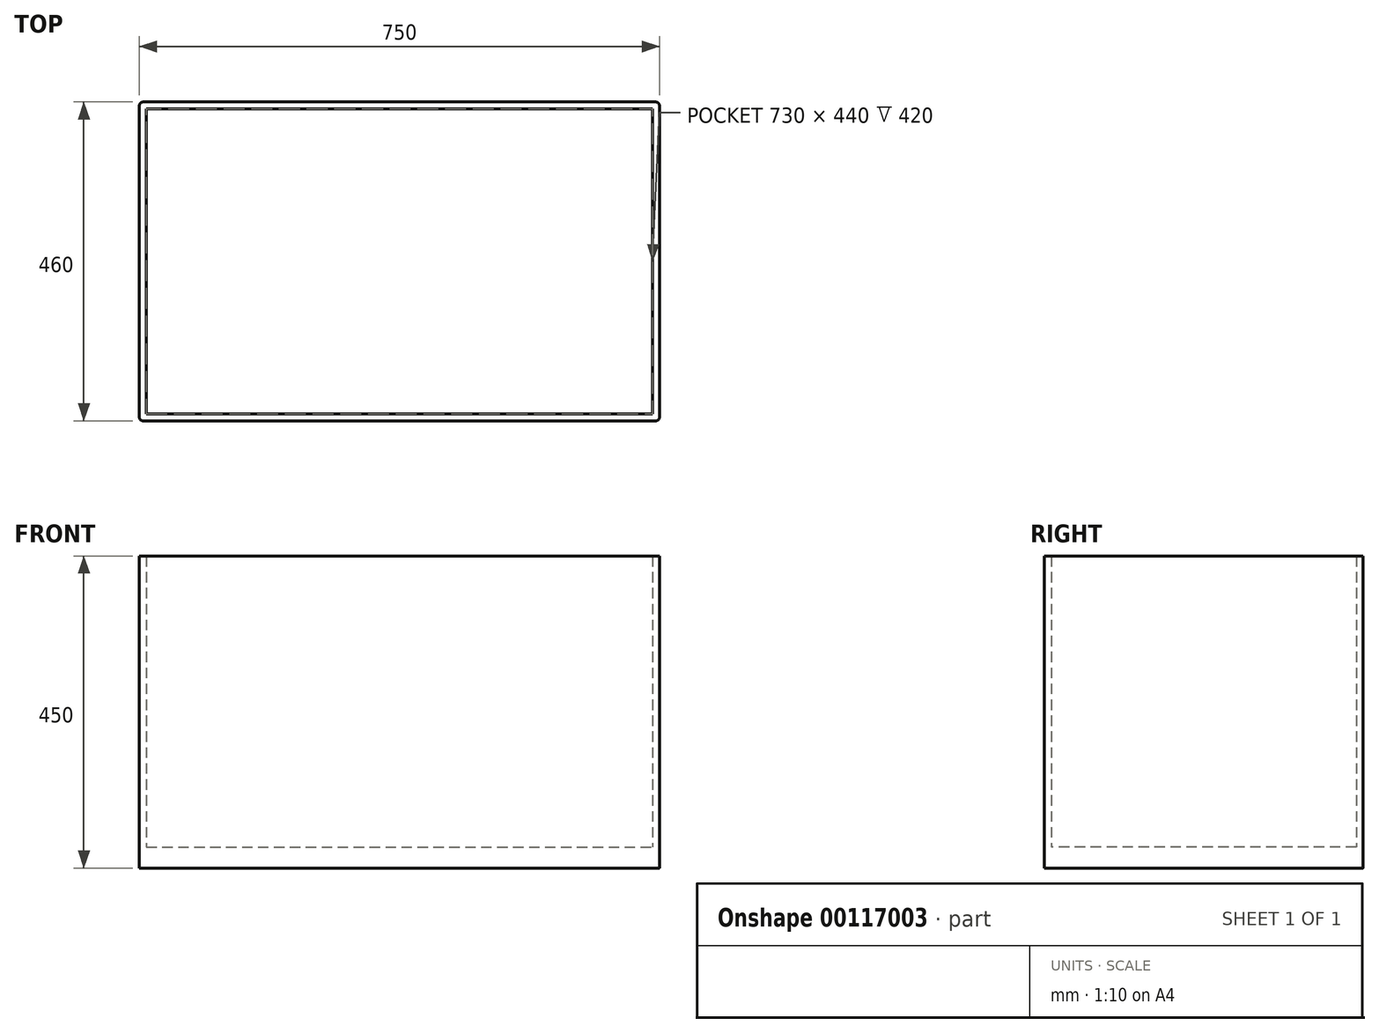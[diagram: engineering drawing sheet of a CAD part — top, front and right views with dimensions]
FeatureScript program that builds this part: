
annotation { "Feature Type Name" : "Feature", "Feature Type Description" : "" }
export const myFeature = defineFeature(function(context is Context, id is Id, definition is map)
    precondition{}
    {
        {
            var Q0;
            Q0=qCreatedBy(makeId("Top.planeOp"),FACE);
            var sketch = newSketch(context, id + "F0", { "sketchPlane" : qUnion([Q0])});
            skLineSegment(sketch, "E0.bottom", {"start": v(-376.94, 230) * mm, "end": v(373.06, 230) * mm});
            skLineSegment(sketch, "E0.top", {"start": v(-376.94, -230) * mm, "end": v(373.06, -230) * mm});
            skLineSegment(sketch, "E0.left", {"start": v(-376.94, 230) * mm, "end": v(-376.94, -230) * mm});
            skLineSegment(sketch, "E0.right", {"start": v(373.06, 230) * mm, "end": v(373.06, -230) * mm});
            skPoint(sketch, "E0.middle", {"position": v(-1.94, 0) * mm});
            skLineSegment(sketch, "E1.0", {"start": v(-366.94, 220) * mm, "end": v(363.06, 220) * mm});
            skLineSegment(sketch, "E1.1", {"start": v(-366.94, 220) * mm, "end": v(-366.94, -220) * mm});
            skLineSegment(sketch, "E1.2", {"start": v(-366.94, -220) * mm, "end": v(363.06, -220) * mm});
            skLineSegment(sketch, "E1.3", {"start": v(363.06, 220) * mm, "end": v(363.06, -220) * mm});
            skSolve(sketch);
        }
        {
            var Q0;
            Q0=makeQuery(id+"F0.imprint","IMPRINT",FACE,{"disambiguationData":[TD([[makeQuery(id+"F0.imprint","IMPRINT",EDGE,{"derivedFrom":sQuery(id+"F0.wireOp",EDGE,"E1.0")}),-1.0]])]});
            extrude(context, id + "F1", {"entities" : qUnion([Q0]), "depth" : 30 * mm});
        }
        {
            var Q0;
            Q0=makeQuery(id+"F0.imprint","IMPRINT",FACE,{"disambiguationData":[TD([[makeQuery(id+"F0.imprint","IMPRINT",EDGE,{"derivedFrom":sQuery(id+"F0.wireOp",EDGE,"E0.bottom")}),-1.0]])]});
            extrude(context, id + "F2", {"entities" : qUnion([Q0]), "operationType" : NewBodyOperationType.ADD, "depth" : 450 * mm});
        }
        {
            var Q0;
            Q0=makeQuery(id+"F2.opExtrude","SWEPT_EDGE",EDGE,{"disambiguationData":[OSD([sQuery(id+"F0.wireOp",EDGE,"E0.top"),sQuery(id+"F0.wireOp",EDGE,"E0.left")])]});
            var Q1;
            Q1=makeQuery(id+"F2.opExtrude","SWEPT_EDGE",EDGE,{"disambiguationData":[OSD([sQuery(id+"F0.wireOp",EDGE,"E0.top"),sQuery(id+"F0.wireOp",EDGE,"E0.right")])]});
            var Q2;
            Q2=makeQuery(id+"F2.opExtrude","SWEPT_EDGE",EDGE,{"disambiguationData":[OSD([sQuery(id+"F0.wireOp",EDGE,"E0.bottom"),sQuery(id+"F0.wireOp",EDGE,"E0.right")])]});
            var Q3;
            Q3=makeQuery(id+"F2.opExtrude","SWEPT_EDGE",EDGE,{"disambiguationData":[OSD([sQuery(id+"F0.wireOp",EDGE,"E0.bottom"),sQuery(id+"F0.wireOp",EDGE,"E0.left")])]});
            fillet(context, id + "F3", {"entities" : qUnion([Q0, Q1, Q2, Q3]), "radius" : 5 * mm, "tangentPropagation" : true, "allowEdgeOverflow" : false});
        }
    });
